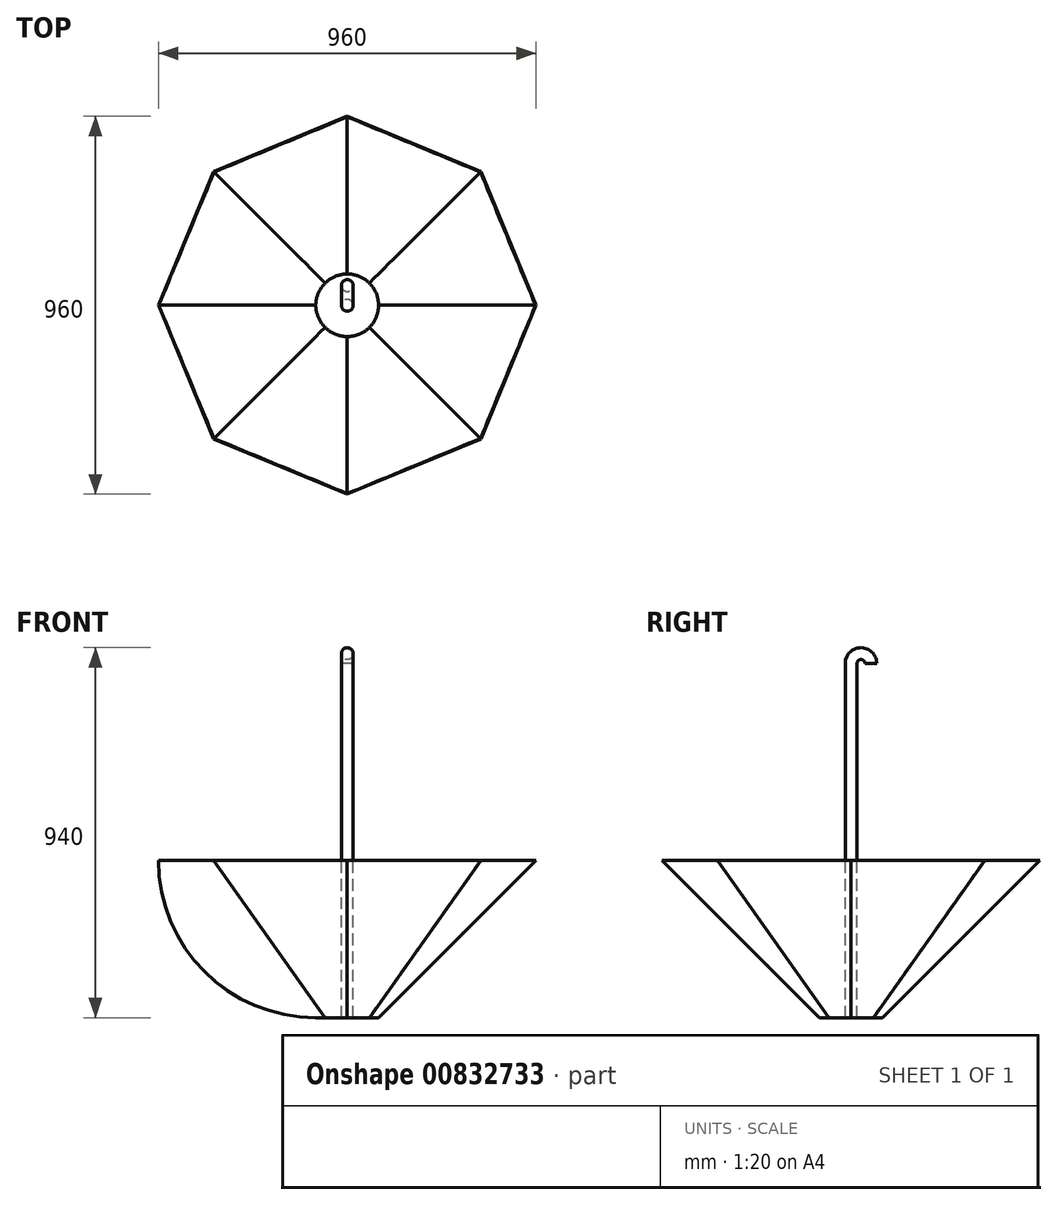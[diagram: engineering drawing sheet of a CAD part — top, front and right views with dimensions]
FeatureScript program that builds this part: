
annotation { "Feature Type Name" : "Feature", "Feature Type Description" : "" }
export const myFeature = defineFeature(function(context is Context, id is Id, definition is map)
    precondition{}
    {
        {
            var Q0;
            Q0=qCreatedBy(makeId("Top.planeOp"),FACE);
            var sketch = newSketch(context, id + "F0", { "sketchPlane" : qUnion([Q0])});
            skCircle(sketch, "E0", {"center": v(0, 0) * mm, "radius": 80 * mm});
            skSolve(sketch);
        }
        {
            var Q0;
            Q0=qCreatedBy(makeId("Top.planeOp"),FACE);
            cPlane(context, id + "F1", {"entities" : qUnion([Q0]), "cplaneType" : CPlaneType.OFFSET, "offset" : 400 * mm, "width" : 150 * mm, "height" : 150 * mm});
        }
        {
            var Q0;
            Q0=qCreatedBy(id+"F1.planeOp",FACE);
            var sketch = newSketch(context, id + "F2", { "sketchPlane" : qUnion([Q0])});
            skCircle(sketch, "E1.cCircle", {"center": v(0, 0) * mm, "radius": 443.46 * mm, "construction": true});
            skLineSegment(sketch, "E1.0", {"start": v(339.41, 339.41) * mm, "end": v(480, 0) * mm});
            skLineSegment(sketch, "E1.1", {"start": v(480, 0) * mm, "end": v(339.41, -339.41) * mm});
            skLineSegment(sketch, "E1.2", {"start": v(339.41, -339.41) * mm, "end": v(0, -480) * mm});
            skLineSegment(sketch, "E1.3", {"start": v(0, -480) * mm, "end": v(-339.41, -339.41) * mm});
            skLineSegment(sketch, "E1.4", {"start": v(-339.41, -339.41) * mm, "end": v(-480, 0) * mm});
            skLineSegment(sketch, "E1.5", {"start": v(-480, 0) * mm, "end": v(-339.41, 339.41) * mm});
            skLineSegment(sketch, "E1.6", {"start": v(-339.41, 339.41) * mm, "end": v(0, 480) * mm});
            skLineSegment(sketch, "E1.7", {"start": v(0, 480) * mm, "end": v(339.41, 339.41) * mm});
            skPoint(sketch, "E1.0.midPoint", {"position": v(409.7, 169.7) * mm});
            skSolve(sketch);
        }
        {
            var Q0;
            Q0=qCreatedBy(makeId("Front.planeOp"),FACE);
            var sketch = newSketch(context, id + "F3", { "sketchPlane" : qUnion([Q0])});
            skArc(sketch, "E2", {"start": v(-480, 400) * mm, "mid": v(-362.84, 117.16) * mm, "end": v(-80, 0) * mm});
            skPoint(sketch, "E3.orphan", {"position": v(-80, 462.28) * mm});
            skSolve(sketch);
        }
        {
            var Q0;
            Q0=makeQuery(id+"F0.imprint","IMPRINT",FACE,{"disambiguationData":[TD([[makeQuery(id+"F0.imprint","IMPRINT",EDGE,{"derivedFrom":sQuery(id+"F0.wireOp",EDGE,"E0")}),1.0]])]});
            var Q1;
            Q1=makeQuery(id+"F2.imprint","IMPRINT",FACE,{"disambiguationData":[TD([[makeQuery(id+"F2.imprint","IMPRINT",EDGE,{"derivedFrom":sQuery(id+"F2.wireOp",EDGE,"E1.0")}),-1.0]])]});
            var Q2;
            Q2=sQuery(id+"FmPlAKZRSuV0m7z_0.5.F3.wireOp",EDGE,"E2");
            var Q3;
            Q3=sQuery(id+"FmPlAKZRSuV0m7z_0.4.F3.wireOp",EDGE,"E2");
            var Q4;
            Q4=sQuery(id+"FmPlAKZRSuV0m7z_0.3.F3.wireOp",EDGE,"E2");
            var Q5;
            Q5=sQuery(id+"FmPlAKZRSuV0m7z_0.2.F3.wireOp",EDGE,"E2");
            var Q6;
            Q6=sQuery(id+"FmPlAKZRSuV0m7z_0.1.F3.wireOp",EDGE,"E2");
            var Q7;
            Q7=sQuery(id+"FmPlAKZRSuV0m7z_0.6.F3.wireOp",EDGE,"E2");
            var Q8;
            Q8=sQuery(id+"FmPlAKZRSuV0m7z_0.7.F3.wireOp",EDGE,"E2");
            var Q9;
            Q9=sQuery(id+"F3.wireOp",EDGE,"E2");
            loft(context, id + "F4", {"addGuides" : true, "sheetProfilesArray" : [{ "sheetProfileEntities" : qUnion([Q0]) }, { "sheetProfileEntities" : qUnion([Q1]) }], "guidesArray" : [{ "guideEntities" : qUnion([Q2]), "guideDerivativeType" : LoftGuideDerivativeType.DEFAULT, "guideDerivativeMagnitude" : 1 }, { "guideEntities" : qUnion([Q3]), "guideDerivativeType" : LoftGuideDerivativeType.DEFAULT, "guideDerivativeMagnitude" : 1 }, { "guideEntities" : qUnion([Q4]), "guideDerivativeType" : LoftGuideDerivativeType.DEFAULT, "guideDerivativeMagnitude" : 1 }, { "guideEntities" : qUnion([Q5]), "guideDerivativeType" : LoftGuideDerivativeType.DEFAULT, "guideDerivativeMagnitude" : 1 }, { "guideEntities" : qUnion([Q6]), "guideDerivativeType" : LoftGuideDerivativeType.DEFAULT, "guideDerivativeMagnitude" : 1 }, { "guideEntities" : qUnion([Q7]), "guideDerivativeType" : LoftGuideDerivativeType.DEFAULT, "guideDerivativeMagnitude" : 1 }, { "guideEntities" : qUnion([Q8]), "guideDerivativeType" : LoftGuideDerivativeType.DEFAULT, "guideDerivativeMagnitude" : 1 }, { "guideEntities" : qUnion([Q9]), "guideDerivativeType" : LoftGuideDerivativeType.DEFAULT, "guideDerivativeMagnitude" : 1 }]});
        }
        {
            var Q0;
            Q0=makeQuery(id+"F4.opLoft","CAP_FACE",FACE,{"disambiguationData":[OSD([makeQuery(id+"F2.imprint","IMPRINT",FACE,{"disambiguationData":[TD([[makeQuery(id+"F2.imprint","IMPRINT",EDGE,{"derivedFrom":sQuery(id+"F2.wireOp",EDGE,"E1.0")}),-1.0]])]})])],"isStart":true});
            shell(context, id + "F5", {"entities" : qUnion([Q0]), "thickness" : 1 * mm});
        }
        {
            var Q0;
            Q0=qCreatedBy(makeId("Right.planeOp"),FACE);
            var sketch = newSketch(context, id + "F6", { "sketchPlane" : qUnion([Q0])});
            skLineSegment(sketch, "E4", {"start": v(0, 0) * mm, "end": v(0, 900) * mm});
            skArc(sketch, "E5", {"start": v(50, 900) * mm, "mid": v(25, 925) * mm, "end": v(0, 900) * mm});
            skSolve(sketch);
        }
        {
            var Q0;
            Q0=makeQuery(id+"F5.opShell","OFFSET_FACE",FACE,{"disambiguationData":[OSD([makeQuery(id+"F0.imprint","IMPRINT",FACE,{"disambiguationData":[TD([[makeQuery(id+"F0.imprint","IMPRINT",EDGE,{"derivedFrom":sQuery(id+"F0.wireOp",EDGE,"E0")}),1.0]])]})])]});
            var sketch = newSketch(context, id + "F7", { "sketchPlane" : qUnion([Q0])});
            skCircle(sketch, "E6", {"center": v(0, 0) * mm, "radius": 15 * mm});
            skSolve(sketch);
        }
        {
            var Q0;
            Q0=makeQuery(id+"F7.imprint","IMPRINT",FACE,{"disambiguationData":[TD([[makeQuery(id+"F7.imprint","IMPRINT",EDGE,{"derivedFrom":sQuery(id+"F7.wireOp",EDGE,"E6")}),1.0]])]});
            var Q1;
            Q1=sQuery(id+"F6.wireOp",EDGE,"E4");
            var Q2;
            Q2=sQuery(id+"F6.wireOp",EDGE,"E5");
            sweep(context, id + "F8", {"profiles" : qUnion([Q0]), "path" : qUnion([Q1, Q2])});
        }
    });
